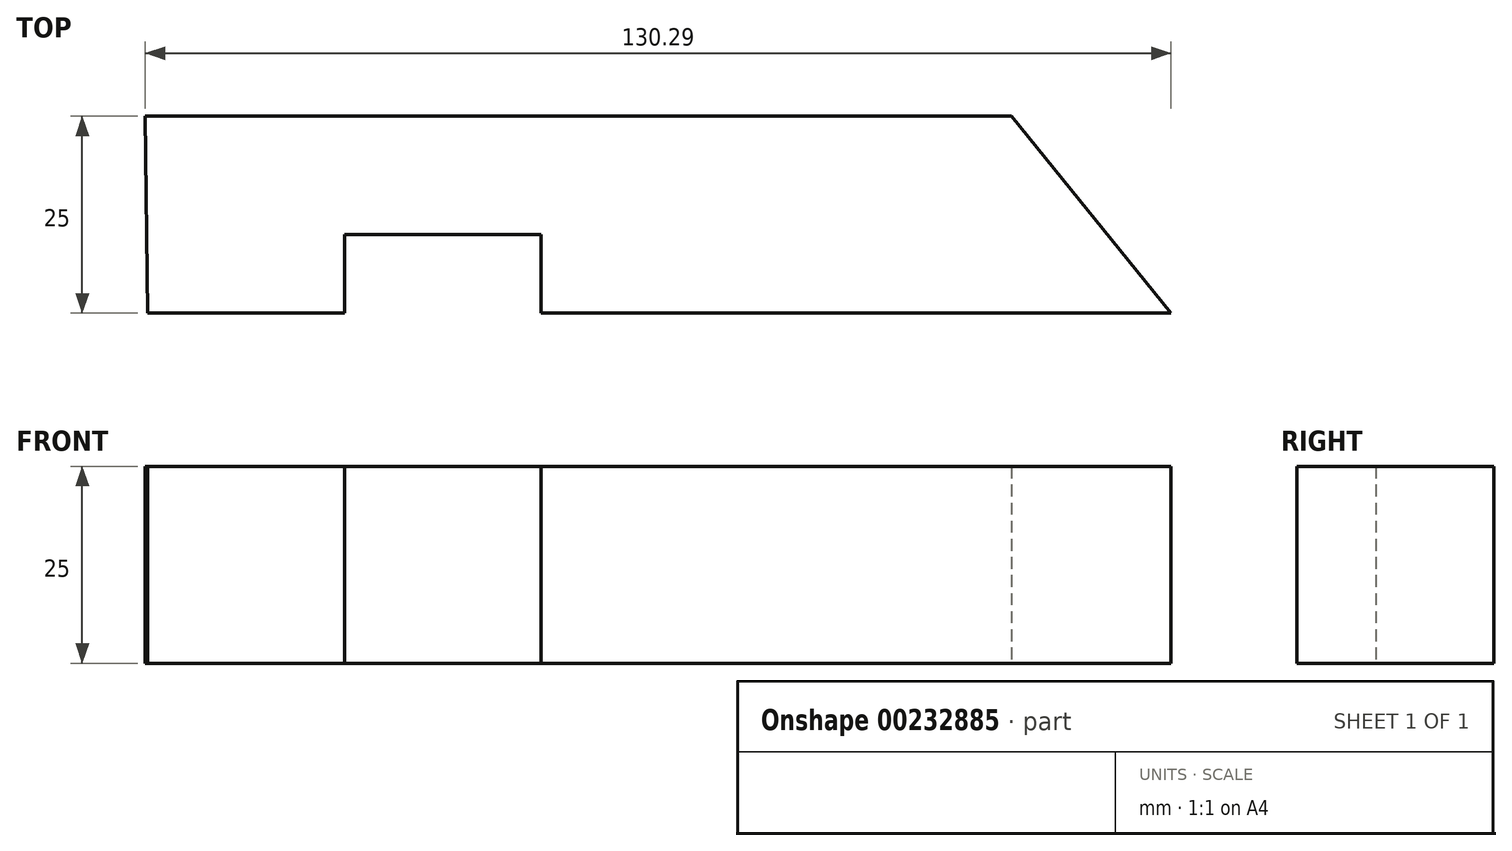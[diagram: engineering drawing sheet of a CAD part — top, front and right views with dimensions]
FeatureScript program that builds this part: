
annotation { "Feature Type Name" : "Feature", "Feature Type Description" : "" }
export const myFeature = defineFeature(function(context is Context, id is Id, definition is map)
    precondition{}
    {
        {
            var Q0;
            Q0=qCreatedBy(makeId("Top.planeOp"),FACE);
            var sketch = newSketch(context, id + "F0", { "sketchPlane" : qUnion([Q0])});
            skLineSegment(sketch, "E0", {"start": v(-81.83, 48.74) * mm, "end": v(28.17, 48.74) * mm});
            skLineSegment(sketch, "E1", {"start": v(28.17, 48.74) * mm, "end": v(48.46, 23.74) * mm});
            skLineSegment(sketch, "E2", {"start": v(48.46, 23.74) * mm, "end": v(-31.54, 23.74) * mm});
            skLineSegment(sketch, "E3", {"start": v(-31.54, 23.74) * mm, "end": v(-31.54, 33.74) * mm});
            skLineSegment(sketch, "E4", {"start": v(-31.54, 33.74) * mm, "end": v(-56.54, 33.74) * mm});
            skLineSegment(sketch, "E5", {"start": v(-56.54, 33.74) * mm, "end": v(-56.54, 23.74) * mm});
            skLineSegment(sketch, "E6", {"start": v(-56.54, 23.74) * mm, "end": v(-81.54, 23.74) * mm});
            skLineSegment(sketch, "E7", {"start": v(-81.54, 23.74) * mm, "end": v(-81.83, 48.74) * mm});
            skSolve(sketch);
        }
        {
            var Q0;
            Q0=makeQuery(id+"F0.imprint","IMPRINT",FACE,{"disambiguationData":[TD([[makeQuery(id+"F0.imprint","IMPRINT",EDGE,{"derivedFrom":sQuery(id+"F0.wireOp",EDGE,"E0")}),-1.0]])]});
            extrude(context, id + "F1", {"entities" : qUnion([Q0]), "depth" : 25 * mm});
        }
    });
